annotation { "Feature Type Name" : "Feature", "Feature Type Description" : "" }
export const myFeature = defineFeature(function(context is Context, id is Id, definition is map)
    precondition{}
    {
        {
            var Q0;
            Q0=qCreatedBy(makeId("Right.planeOp"),FACE);
            var sketch = newSketch(context, id + "F0", { "sketchPlane" : qUnion([Q0])});
            skLineSegment(sketch, "E0.bottom", {"start": v(-33, 0) * mm, "end": v(0, 0) * mm});
            skLineSegment(sketch, "E0.top", {"start": v(-33, 16) * mm, "end": v(-28, 16) * mm});
            skLineSegment(sketch, "E0.left", {"start": v(-33, 0) * mm, "end": v(-33, 16) * mm});
            skLineSegment(sketch, "E0.right", {"start": v(0, 0) * mm, "end": v(0, 27) * mm});
            skLineSegment(sketch, "E1.top", {"start": v(-28, 12) * mm, "end": v(-20, 12) * mm});
            skLineSegment(sketch, "E1.left", {"start": v(-28, 16) * mm, "end": v(-28, 12) * mm});
            skLineSegment(sketch, "E1.right", {"start": v(-20, 27) * mm, "end": v(-20, 12) * mm});
            skLineSegment(sketch, "E2.trimOffspring", {"start": v(-20, 27) * mm, "end": v(0, 27) * mm});
            skSolve(sketch);
        }
        {
            var Q0;
            Q0=makeQuery(id+"F0.imprint","IMPRINT",FACE,{"disambiguationData":[TD([[makeQuery(id+"F0.imprint","IMPRINT",EDGE,{"derivedFrom":sQuery(id+"F0.wireOp",EDGE,"E0.bottom")}),1.0]])]});
            extrude(context, id + "F1", {"entities" : qUnion([Q0]), "depth" : 147 * mm, "offsetDistance" : 25 * mm});
        }
        {
            var Q0;
            Q0=makeQuery(id+"F1.opExtrude","SWEPT_FACE",FACE,{"disambiguationData":[OSD([sQuery(id+"F0.wireOp",EDGE,"E1.top")])]});
            var sketch = newSketch(context, id + "F2", { "sketchPlane" : qUnion([Q0])});
            skArc(sketch, "E3", {"start": v(82.85, -26.05) * mm, "mid": v(84.9, -24) * mm, "end": v(82.85, -21.95) * mm});
            skArc(sketch, "E4", {"start": v(65.55, -21.95) * mm, "mid": v(63.5, -24) * mm, "end": v(65.55, -26.05) * mm});
            skLineSegment(sketch, "E5", {"start": v(65.55, -26.05) * mm, "end": v(82.85, -26.05) * mm});
            skLineSegment(sketch, "E6", {"start": v(65.55, -21.95) * mm, "end": v(82.85, -21.95) * mm});
            skSolve(sketch);
        }
        {
            var Q0;
            Q0=makeQuery(id+"F2.imprint","IMPRINT",FACE,{"disambiguationData":[TD([[makeQuery(id+"F2.imprint","IMPRINT",EDGE,{"derivedFrom":sQuery(id+"F2.wireOp",EDGE,"E3")}),1.0]])]});
            extrude(context, id + "F3", {"entities" : qUnion([Q0]), "operationType" : NewBodyOperationType.REMOVE, "endBound" : BoundingType.THROUGH_ALL, "oppositeDirection" : true, "depth" : 25 * mm, "offsetDistance" : 25 * mm});
        }
        {
            var Q0;
            Q0=makeQuery(id+"F1.opExtrude","SWEPT_FACE",FACE,{"disambiguationData":[OSD([sQuery(id+"F0.wireOp",EDGE,"E2.trimOffspring")])]});
            var sketch = newSketch(context, id + "F4", { "sketchPlane" : qUnion([Q0])});
            skText(sketch, "E7", { "text": "TOTAL NONSENSE", "fontName": "OpenSans-Bold.ttf"});
            const initialGuessF4  = {"E7": [0.00087, -0.0157, 1, 0, 0.0117]};
            skSetInitialGuess(sketch, initialGuessF4);
            skSolve(sketch);
        }
        {
            var Q0;
            Q0 = qSketchRegion(id + "F4", true);
            extrude(context, id + "F5", {"entities" : qUnion([Q0]), "operationType" : NewBodyOperationType.REMOVE, "oppositeDirection" : true, "depth" : 1 * mm, "offsetDistance" : 25 * mm});
        }
        {
            var Q0;
            Q0=makeQuery(id+"F1.opExtrude","SWEPT_FACE",FACE,{"disambiguationData":[OSD([sQuery(id+"F0.wireOp",EDGE,"E0.bottom")])]});
            var sketch = newSketch(context, id + "F6", { "sketchPlane" : qUnion([Q0])});
            skLineSegment(sketch, "E8.bottom", {"start": v(41.5, 27.4) * mm, "end": v(86.9, 27.4) * mm});
            skLineSegment(sketch, "E8.top", {"start": v(41.5, 20.6) * mm, "end": v(44.94, 20.6) * mm});
            skLineSegment(sketch, "E8.left", {"start": v(38.5, 24.4) * mm, "end": v(38.5, 23.6) * mm});
            skLineSegment(sketch, "E8.right", {"start": v(89.9, 24.4) * mm, "end": v(89.9, 23.6) * mm});
            skPoint(sketch, "E9.visualSharp", {"position": v(89.9, 27.4) * mm});
            skArc(sketch, "E9.filletArc", {"start": v(89.9, 24.4) * mm, "mid": v(89.02, 26.52) * mm, "end": v(86.9, 27.4) * mm});
            skPoint(sketch, "E10.visualSharp", {"position": v(89.9, 20.6) * mm});
            skArc(sketch, "E10.filletArc", {"start": v(86.9, 20.6) * mm, "mid": v(89.02, 21.48) * mm, "end": v(89.9, 23.6) * mm});
            skPoint(sketch, "E11.visualSharp", {"position": v(38.5, 20.6) * mm});
            skArc(sketch, "E11.filletArc", {"start": v(38.5, 23.6) * mm, "mid": v(39.38, 21.48) * mm, "end": v(41.5, 20.6) * mm});
            skPoint(sketch, "E12.visualSharp", {"position": v(38.5, 27.4) * mm});
            skArc(sketch, "E12.filletArc", {"start": v(41.5, 27.4) * mm, "mid": v(39.38, 26.52) * mm, "end": v(38.5, 24.4) * mm});
            skLineSegment(sketch, "E13.top", {"start": v(44.94, 0) * mm, "end": v(51.24, 0) * mm});
            skLineSegment(sketch, "E13.left", {"start": v(44.94, 20.6) * mm, "end": v(44.94, 0) * mm});
            skLineSegment(sketch, "E13.right", {"start": v(51.24, 20.6) * mm, "end": v(51.24, 0) * mm});
            skLineSegment(sketch, "E14.trimOffspring", {"start": v(51.24, 20.6) * mm, "end": v(86.9, 20.6) * mm});
            skSolve(sketch);
        }
        {
            var Q0;
            Q0 = qSketchRegion(id + "F6", true);
            extrude(context, id + "F7", {"entities" : qUnion([Q0]), "operationType" : NewBodyOperationType.REMOVE, "oppositeDirection" : true, "depth" : 9.9 * mm, "offsetDistance" : 25 * mm});
        }
        {
            var Q0;
            Q0=makeQuery(id+"F1.opExtrude","SWEPT_FACE",FACE,{"disambiguationData":[OSD([sQuery(id+"F0.wireOp",EDGE,"E0.left")])]});
            var sketch = newSketch(context, id + "F8", { "sketchPlane" : qUnion([Q0])});
            skCircle(sketch, "E15", {"center": v(53.5, 6.6) * mm, "radius": 3 * mm});
            skSolve(sketch);
        }
        {
            var Q0;
            Q0=makeQuery(id+"F8.imprint","IMPRINT",FACE,{"disambiguationData":[TD([[makeQuery(id+"F8.imprint","IMPRINT",EDGE,{"derivedFrom":sQuery(id+"F8.wireOp",EDGE,"E15")}),1.0]])]});
            extrude(context, id + "F9", {"entities" : qUnion([Q0]), "operationType" : NewBodyOperationType.REMOVE, "endBound" : BoundingType.UP_TO_NEXT, "oppositeDirection" : true, "depth" : 25 * mm, "offsetDistance" : 25 * mm});
        }
    });